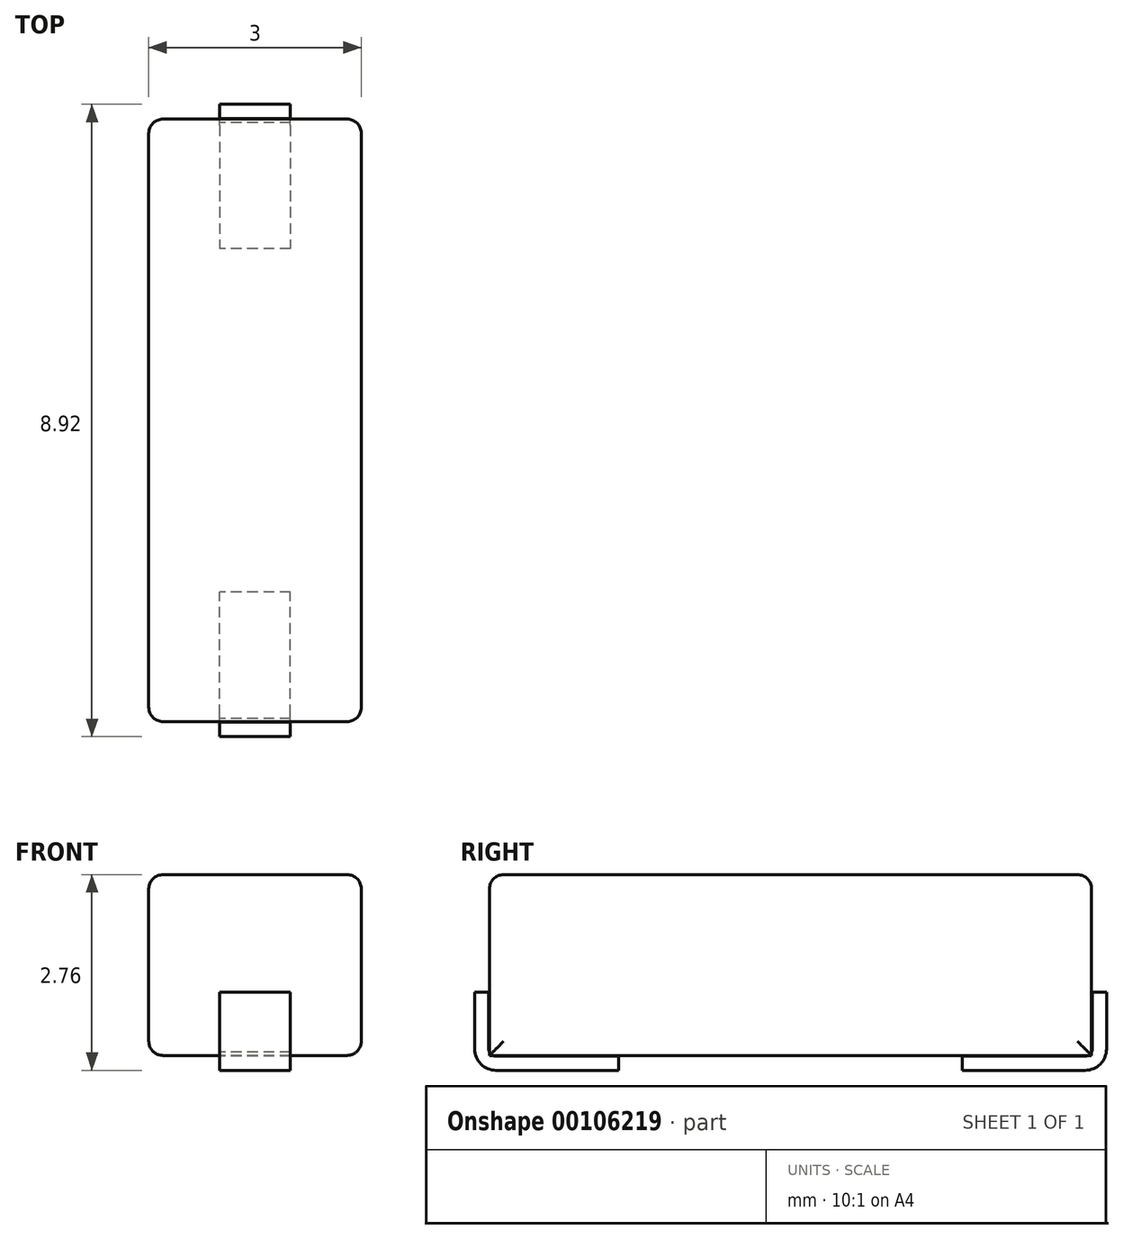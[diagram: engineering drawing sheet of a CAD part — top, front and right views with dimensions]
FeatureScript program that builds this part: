
annotation { "Feature Type Name" : "Feature", "Feature Type Description" : "" }
export const myFeature = defineFeature(function(context is Context, id is Id, definition is map)
    precondition{}
    {
        {
            var Q0;
            Q0=qCreatedBy(makeId("Front.planeOp"),FACE);
            var sketch = newSketch(context, id + "F0", { "sketchPlane" : qUnion([Q0])});
            skLineSegment(sketch, "E0.bottom", {"start": v(-1.5, 2.55) * mm, "end": v(1.5, 2.55) * mm});
            skLineSegment(sketch, "E0.top", {"start": v(-1.5, 0) * mm, "end": v(1.5, 0) * mm});
            skLineSegment(sketch, "E0.left", {"start": v(-1.5, 2.55) * mm, "end": v(-1.5, 0) * mm});
            skLineSegment(sketch, "E0.right", {"start": v(1.5, 2.55) * mm, "end": v(1.5, 0) * mm});
            skSolve(sketch);
        }
        {
            var Q0;
            Q0=makeQuery(id+"F0.imprint","IMPRINT",FACE,{"disambiguationData":[TD([[makeQuery(id+"F0.imprint","IMPRINT",EDGE,{"derivedFrom":sQuery(id+"F0.wireOp",EDGE,"E0.bottom")}),-1.0]])]});
            extrude(context, id + "F1", {"entities" : qUnion([Q0]), "endBound" : BoundingType.SYMMETRIC, "depth" : 8.5 * mm});
        }
        {
            var Q0;
            Q0=qCreatedBy(makeId("Right.planeOp"),FACE);
            var sketch = newSketch(context, id + "F2", { "sketchPlane" : qUnion([Q0])});
            skLineSegment(sketch, "E1", {"start": v(-4.26, 0.89) * mm, "end": v(-4.26, 0.1) * mm});
            skLineSegment(sketch, "E2", {"start": v(-4.16, 0) * mm, "end": v(-2.43, 0) * mm});
            skPoint(sketch, "E3.visualSharp", {"position": v(-4.26, 0) * mm});
            skArc(sketch, "E3.filletArc", {"start": v(-4.26, 0.09) * mm, "mid": v(-4.23, 0.02) * mm, "end": v(-4.16, 0) * mm});
            skLineSegment(sketch, "E4.0", {"start": v(-4.16, -0.2) * mm, "end": v(-2.43, -0.2) * mm});
            skArc(sketch, "E4.1", {"start": v(-4.46, 0.09) * mm, "mid": v(-4.37, -0.12) * mm, "end": v(-4.16, -0.2) * mm});
            skLineSegment(sketch, "E4.2", {"start": v(-4.46, 0.89) * mm, "end": v(-4.46, 0.09) * mm});
            skLineSegment(sketch, "E5", {"start": v(-4.46, 0.89) * mm, "end": v(-4.26, 0.89) * mm});
            skLineSegment(sketch, "E6", {"start": v(-2.43, -0.2) * mm, "end": v(-2.43, 0) * mm});
            skLineSegment(sketch, "E7.MirrorCS", {"start": v(4.46, 0.89) * mm, "end": v(4.26, 0.89) * mm});
            skLineSegment(sketch, "E8.MirrorCS", {"start": v(4.46, 0.89) * mm, "end": v(4.46, 0.09) * mm});
            skArc(sketch, "E9.MirrorCS", {"start": v(4.46, 0.09) * mm, "mid": v(4.37, -0.12) * mm, "end": v(4.16, -0.2) * mm});
            skLineSegment(sketch, "E10.MirrorCS", {"start": v(4.16, -0.2) * mm, "end": v(2.43, -0.2) * mm});
            skLineSegment(sketch, "E11.MirrorCS", {"start": v(2.43, -0.2) * mm, "end": v(2.43, 0) * mm});
            skLineSegment(sketch, "E12.MirrorCS", {"start": v(4.16, 0) * mm, "end": v(2.43, 0) * mm});
            skArc(sketch, "E13.MirrorCS", {"start": v(4.26, 0.09) * mm, "mid": v(4.23, 0.02) * mm, "end": v(4.16, 0) * mm});
            skLineSegment(sketch, "E14.MirrorCS", {"start": v(4.26, 0.89) * mm, "end": v(4.26, 0.1) * mm});
            skSolve(sketch);
        }
        {
            var Q0;
            Q0=makeQuery(id+"F2.imprint","IMPRINT",FACE,{"disambiguationData":[TD([[makeQuery(id+"F2.imprint","IMPRINT",EDGE,{"derivedFrom":sQuery(id+"F2.wireOp",EDGE,"E1")}),-1.0]])]});
            var Q1;
            Q1=makeQuery(id+"F2.imprint","IMPRINT",FACE,{"disambiguationData":[TD([[makeQuery(id+"F2.imprint","IMPRINT",EDGE,{"derivedFrom":sQuery(id+"F2.wireOp",EDGE,"E7.MirrorCS")}),1.0]])]});
            extrude(context, id + "F3", {"entities" : qUnion([Q0, Q1]), "operationType" : NewBodyOperationType.ADD, "endBound" : BoundingType.SYMMETRIC, "depth" : 1 * mm});
        }
        {
            var Q0;
            Q0=makeQuery(id+"F1.opExtrude","SWEPT_FACE",FACE,{"disambiguationData":[OSD([sQuery(id+"F0.wireOp",EDGE,"E0.right")])]});
            var Q1;
            Q1=makeQuery(id+"F1.opExtrude","SWEPT_FACE",FACE,{"disambiguationData":[OSD([sQuery(id+"F0.wireOp",EDGE,"E0.left")])]});
            var Q2;
            Q2=makeQuery(id+"F1.opExtrude","SWEPT_FACE",FACE,{"disambiguationData":[OSD([sQuery(id+"F0.wireOp",EDGE,"E0.bottom")])]});
            fillet(context, id + "F4", {"entities" : qUnion([Q0, Q1, Q2]), "radius" : 0.2 * mm, "tangentPropagation" : true, "allowEdgeOverflow" : false});
        }
    });
